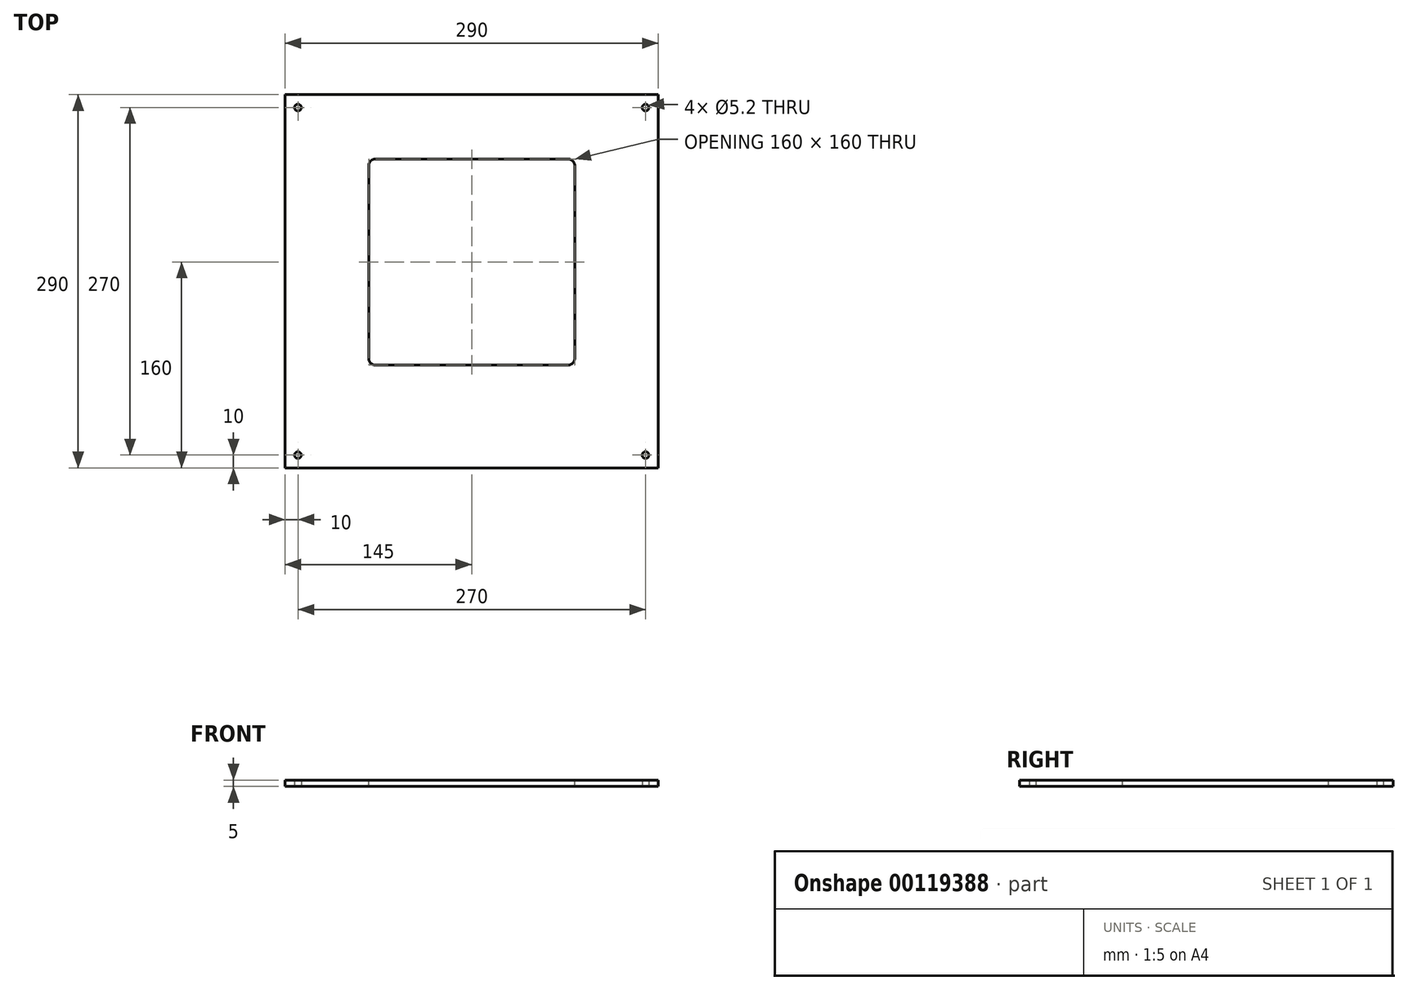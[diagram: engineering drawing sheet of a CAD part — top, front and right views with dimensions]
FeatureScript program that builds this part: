
annotation { "Feature Type Name" : "Feature", "Feature Type Description" : "" }
export const myFeature = defineFeature(function(context is Context, id is Id, definition is map)
    precondition{}
    {
        {
            var Q0;
            Q0=qCreatedBy(makeId("Top.planeOp"),FACE);
            var sketch = newSketch(context, id + "F0", { "sketchPlane" : qUnion([Q0])});
            skLineSegment(sketch, "E0.bottom", {"start": v(145, -145) * mm, "end": v(-145, -145) * mm});
            skLineSegment(sketch, "E0.top", {"start": v(145, 145) * mm, "end": v(-145, 145) * mm});
            skLineSegment(sketch, "E0.left", {"start": v(145, -145) * mm, "end": v(145, 145) * mm});
            skLineSegment(sketch, "E0.right", {"start": v(-145, -145) * mm, "end": v(-145, 145) * mm});
            skPoint(sketch, "E0.middle", {"position": v(0, 0) * mm});
            skCircle(sketch, "E1", {"center": v(-135, 135) * mm, "radius": 2.6 * mm});
            skCircle(sketch, "E2.0.1.0", {"center": v(-135, -135) * mm, "radius": 2.6 * mm});
            skCircle(sketch, "E2.1.0.0", {"center": v(135, 135) * mm, "radius": 2.6 * mm});
            skCircle(sketch, "E2.1.1.0", {"center": v(135, -135) * mm, "radius": 2.6 * mm});
            skLineSegment(sketch, "E2.direction1", {"start": v(-135, 135) * mm, "end": v(135, 135) * mm, "construction": true});
            skLineSegment(sketch, "E2.direction2", {"start": v(-135, 135) * mm, "end": v(-135, -135) * mm, "construction": true});
            skSolve(sketch);
        }
        {
            var Q0;
            Q0=makeQuery(id+"F0.imprint","IMPRINT",FACE,{"disambiguationData":[TD([[makeQuery(id+"F0.imprint","IMPRINT",EDGE,{"derivedFrom":sQuery(id+"F0.wireOp",EDGE,"E0.bottom")}),-1.0]])]});
            extrude(context, id + "F1", {"entities" : qUnion([Q0]), "depth" : 5 * mm});
        }
        {
            var Q0;
            Q0=makeQuery(id+"F1.opExtrude","CAP_FACE",FACE,{"disambiguationData":[OSD([sQuery(id+"F0.wireOp",EDGE,"E0.bottom"),sQuery(id+"F0.wireOp",EDGE,"E0.top"),sQuery(id+"F0.wireOp",EDGE,"E0.left"),sQuery(id+"F0.wireOp",EDGE,"E0.right"),sQuery(id+"F0.wireOp",EDGE,"E1"),sQuery(id+"F0.wireOp",EDGE,"E2.0.1.0"),sQuery(id+"F0.wireOp",EDGE,"E2.1.0.0"),sQuery(id+"F0.wireOp",EDGE,"E2.1.1.0")])],"isStart":false});
            var sketch = newSketch(context, id + "F2", { "sketchPlane" : qUnion([Q0])});
            skLineSegment(sketch, "E3.bottom", {"start": v(75, -65) * mm, "end": v(-75, -65) * mm});
            skLineSegment(sketch, "E3.top", {"start": v(75, 95) * mm, "end": v(-75, 95) * mm});
            skLineSegment(sketch, "E3.left", {"start": v(80, -60) * mm, "end": v(80, 90) * mm});
            skLineSegment(sketch, "E3.right", {"start": v(-80, -60) * mm, "end": v(-80, 90) * mm});
            skPoint(sketch, "E3.middle", {"position": v(0, 0) * mm});
            skPoint(sketch, "E4.visualSharp", {"position": v(-80, 95) * mm});
            skArc(sketch, "E4.filletArc", {"start": v(-75, 95) * mm, "mid": v(-78.54, 93.54) * mm, "end": v(-80, 90) * mm});
            skPoint(sketch, "E5.visualSharp", {"position": v(80, 95) * mm});
            skArc(sketch, "E5.filletArc", {"start": v(80, 90) * mm, "mid": v(78.54, 93.54) * mm, "end": v(75, 95) * mm});
            skPoint(sketch, "E6.visualSharp", {"position": v(80, -65) * mm});
            skArc(sketch, "E6.filletArc", {"start": v(75, -65) * mm, "mid": v(78.54, -63.54) * mm, "end": v(80, -60) * mm});
            skPoint(sketch, "E7.visualSharp", {"position": v(-80, -65) * mm});
            skArc(sketch, "E7.filletArc", {"start": v(-80, -60) * mm, "mid": v(-78.54, -63.54) * mm, "end": v(-75, -65) * mm});
            skSolve(sketch);
        }
        {
            var Q0;
            Q0=makeQuery(id+"F2.imprint","IMPRINT",FACE,{"disambiguationData":[TD([[makeQuery(id+"F2.imprint","IMPRINT",EDGE,{"derivedFrom":sQuery(id+"F2.wireOp",EDGE,"E3.bottom")}),-1.0]])]});
            extrude(context, id + "F3", {"entities" : qUnion([Q0]), "operationType" : NewBodyOperationType.REMOVE, "endBound" : BoundingType.THROUGH_ALL, "oppositeDirection" : true, "depth" : 25 * mm});
        }
    });
